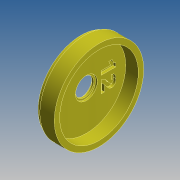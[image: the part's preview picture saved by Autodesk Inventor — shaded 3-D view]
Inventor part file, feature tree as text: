
AUTODESK INVENTOR PART (.ipt)
format: ipt  version: 2015 SP1 (Build 190203100, 203)  size: 259,584 bytes
history: native  units: mm
features: sketch x2, revolve x1, extrude x1
ambient origin geometry x8: Origin, YZ Plane, XZ Plane, XY Plane, X Axis, Y Axis, Z Axis, Center Point
bodies: Solid1 (feature_tree)
feature tree (4):
  revolve  "Revolution1"  [1 undecoded]
  extrude  "Extrusion1"  Depth=2.0mm
  sketch  "Sketch1"  dims[d0=49.8mm d1=47.8mm]
  sketch  "Sketch2"  dims[d2=10.0mm d3=1.0mm d4=2.0mm d7=3.0mm d8=3.0mm d10=10.0mm d11=90.0deg d17=12.2mm d18=1.5mm d19=0.0mm d20=1.0mm d21=1.0mm]
note: 1 required parameter value undecoded (feature->parameter linkage not recoverable at this tier; creation-order binding heuristic only, values carry confidence <= 0.55)
